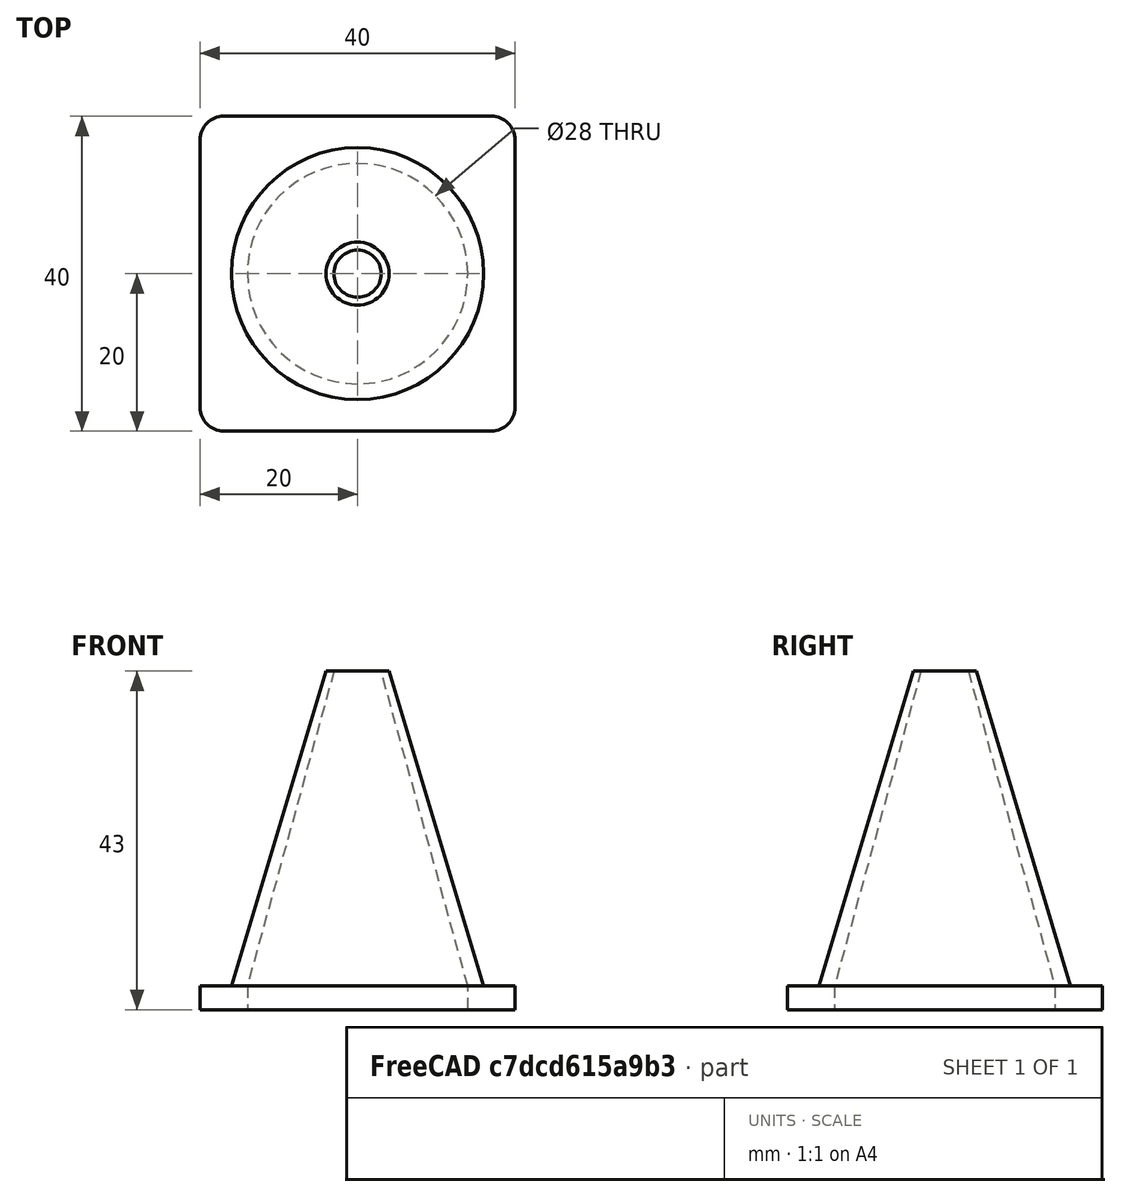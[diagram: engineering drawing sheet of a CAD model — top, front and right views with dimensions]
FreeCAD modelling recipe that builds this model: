
FCSTD DOCUMENT  (FreeCAD 0.21R33694 (Git))
Label: OJT1_T014_Con
License: All rights reserved
LicenseURL: https://en.wikipedia.org/wiki/All_rights_reserved
objects: Part::Cone×2, Part::Cut×2, Part::Box×1, Part::Cylinder×1, Part::Fillet×1
note: 7 computed .brp shape members not serialized (recipe doc carries the construction recipe); baked Part::Feature solids carry a one-line shape summary decoded from their .brp

FEATURE [Part::Cone] Cone  label="Con"
  Angle = 360
  AttacherType = Attacher::AttachEngine3D
  Height = 40
  Radius1 = 16
  Radius2 = 4
FEATURE [Part::Cone] Cone001  label="Con001"
  Angle = 360
  AttacherType = Attacher::AttachEngine3D
  Height = 40
  Radius1 = 14
  Radius2 = 3
FEATURE [Part::Cut] Cut
  Base = -> Cone
  Tool = -> Cone001
FEATURE [Part::Box] Box  label="Cub"
  AttacherType = Attacher::AttachEngine3D
  Height = 3
  Length = 40
  Placement = pos=(-20,-20,-3) rot=(0,0,1;0rad)
  Width = 40
  expr: .Placement.Base.x = -20
  expr: .Placement.Base.y = -20 mm
FEATURE [Part::Cylinder] Cylinder  label="Cilindre"
  Angle = 360
  AttacherType = Attacher::AttachEngine3D
  FirstAngle = 0
  Height = 3
  Placement = pos=(0,0,-3) rot=(0,0,1;0rad)
  Radius = 14
  SecondAngle = 0
FEATURE [Part::Cut] Cut001
  Base = -> Box
  Tool = -> Cylinder
FEATURE [Part::Fillet] Fillet
  Base = -> Cut001
  Edges = 4 edges r=3: [Edge1,Edge3,Edge6,Edge12]
